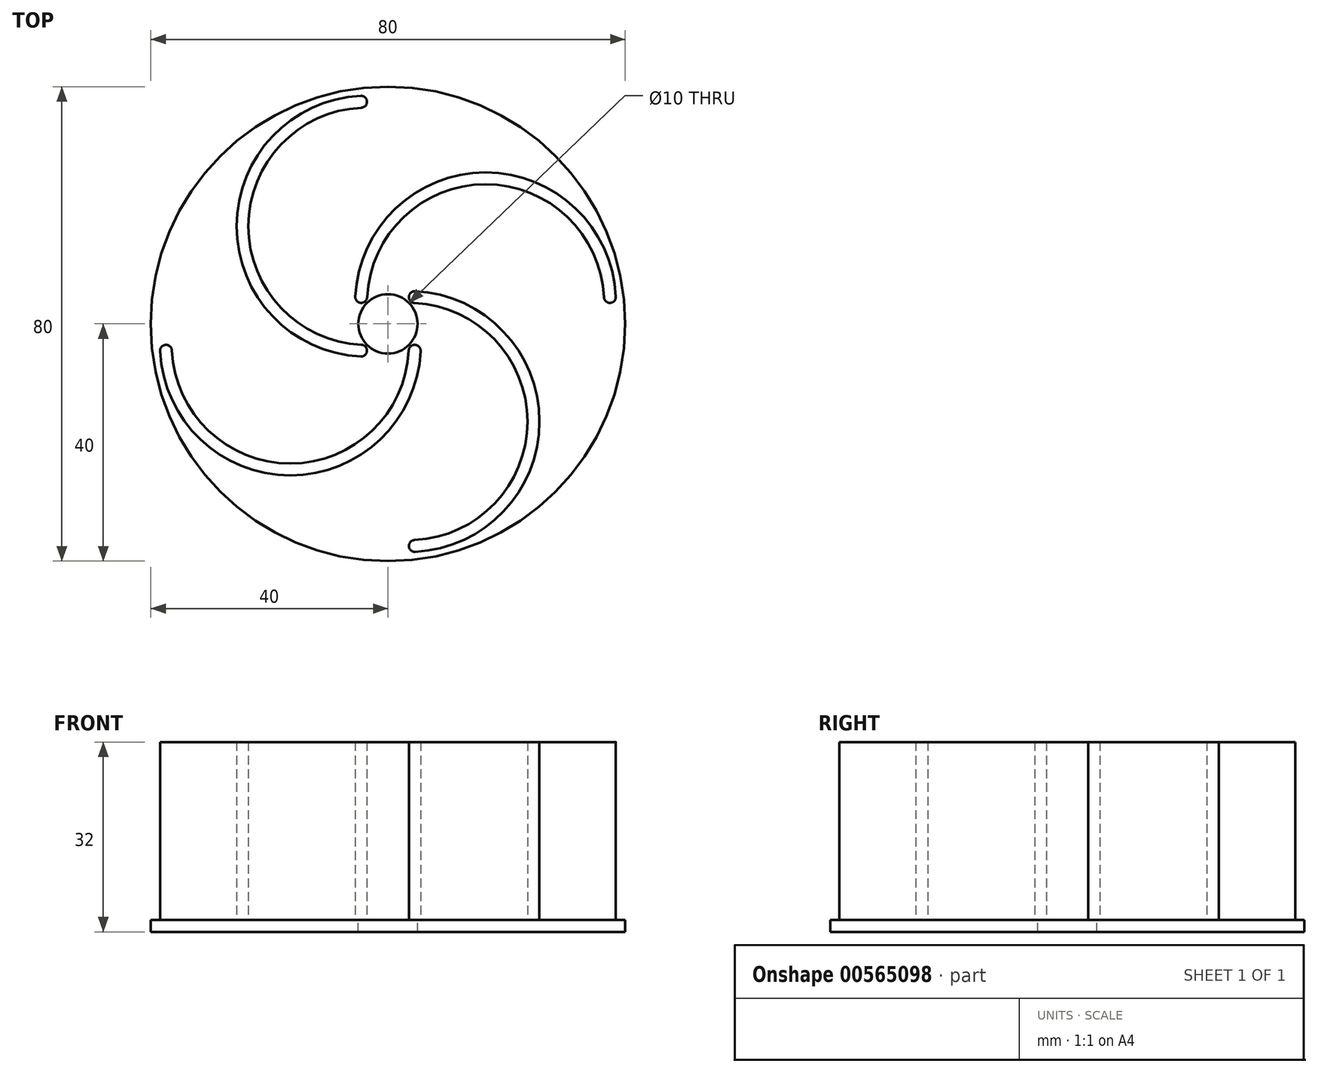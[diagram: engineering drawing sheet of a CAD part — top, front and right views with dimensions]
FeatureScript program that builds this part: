
annotation { "Feature Type Name" : "Feature", "Feature Type Description" : "" }
export const myFeature = defineFeature(function(context is Context, id is Id, definition is map)
    precondition{}
    {
        {
            var Q0;
            Q0=qCreatedBy(makeId("Top.planeOp"),FACE);
            var sketch = newSketch(context, id + "F0", { "sketchPlane" : qUnion([Q0])});
            skCircle(sketch, "E0", {"center": v(0, 0) * mm, "radius": 5 * mm});
            skPoint(sketch, "E1", {"position": v(0, 5) * mm});
            skPoint(sketch, "E2", {"position": v(5, 0) * mm});
            skPoint(sketch, "E3", {"position": v(0, -5) * mm});
            skPoint(sketch, "E4", {"position": v(-5, 0) * mm});
            skLineSegment(sketch, "E5", {"start": v(0, 0) * mm, "end": v(-3.54, -3.54) * mm});
            skLineSegment(sketch, "E6", {"start": v(0, 0) * mm, "end": v(-3.54, 3.54) * mm});
            skLineSegment(sketch, "E7", {"start": v(0, 0) * mm, "end": v(3.54, 3.54) * mm});
            skLineSegment(sketch, "E8", {"start": v(0, 0) * mm, "end": v(3.54, -3.54) * mm});
            skArc(sketch, "E9", {"start": v(3.54, -36.46) * mm, "mid": v(23.54, -16.46) * mm, "end": v(3.54, 3.54) * mm});
            skLineSegment(sketch, "E10", {"start": v(-3.54, -3.54) * mm, "end": v(-3.54, 3.54) * mm});
            skLineSegment(sketch, "E11", {"start": v(3.54, 3.54) * mm, "end": v(3.54, -3.54) * mm});
            skLineSegment(sketch, "E12", {"start": v(3.54, -3.54) * mm, "end": v(-3.54, -3.54) * mm});
            skLineSegment(sketch, "E13", {"start": v(-3.54, 3.54) * mm, "end": v(3.54, 3.54) * mm});
            skArc(sketch, "E14", {"start": v(-3.54, 36.46) * mm, "mid": v(-23.54, 16.46) * mm, "end": v(-3.54, -3.54) * mm});
            skArc(sketch, "E15", {"start": v(36.46, 3.54) * mm, "mid": v(16.46, 23.54) * mm, "end": v(-3.54, 3.54) * mm});
            skArc(sketch, "E16", {"start": v(-36.46, -3.54) * mm, "mid": v(-16.46, -23.54) * mm, "end": v(3.54, -3.54) * mm});
            skArc(sketch, "E17.0", {"start": v(38.46, 3.54) * mm, "mid": v(16.46, 25.54) * mm, "end": v(-5.54, 3.54) * mm});
            skArc(sketch, "E18.0", {"start": v(-3.54, 38.46) * mm, "mid": v(-25.54, 16.46) * mm, "end": v(-3.54, -5.54) * mm});
            skArc(sketch, "E19.0", {"start": v(-38.46, -3.54) * mm, "mid": v(-16.46, -25.54) * mm, "end": v(5.54, -3.54) * mm});
            skArc(sketch, "E20.0", {"start": v(3.54, -38.46) * mm, "mid": v(25.54, -16.46) * mm, "end": v(3.54, 5.54) * mm});
            skLineSegment(sketch, "E21", {"start": v(-3.54, 3.54) * mm, "end": v(-5.54, 3.54) * mm});
            skLineSegment(sketch, "E22", {"start": v(-3.54, -5.54) * mm, "end": v(-3.54, -3.54) * mm});
            skLineSegment(sketch, "E23", {"start": v(5.54, -3.54) * mm, "end": v(3.54, -3.54) * mm});
            skLineSegment(sketch, "E24", {"start": v(3.54, 5.54) * mm, "end": v(3.54, 3.54) * mm});
            skLineSegment(sketch, "E25", {"start": v(38.46, 3.54) * mm, "end": v(36.46, 3.54) * mm});
            skLineSegment(sketch, "E26", {"start": v(-3.54, 38.46) * mm, "end": v(-3.54, 36.46) * mm});
            skLineSegment(sketch, "E27", {"start": v(-38.46, -3.54) * mm, "end": v(-36.46, -3.54) * mm});
            skLineSegment(sketch, "E28", {"start": v(3.54, -36.46) * mm, "end": v(3.54, -38.46) * mm});
            skCircle(sketch, "E29", {"center": v(0, 0) * mm, "radius": 40 * mm});
            skSolve(sketch);
        }
        {
            var Q0;
            Q0=makeQuery(id+"F0.imprint","IMPRINT",FACE,{"disambiguationData":[TD([[makeQuery(id+"F0.imprint","IMPRINT",EDGE,{"derivedFrom":sQuery(id+"F0.wireOp",EDGE,"E15")}),-1.0]])]});
            var Q1;
            Q1=makeQuery(id+"F0.imprint","IMPRINT",FACE,{"disambiguationData":[TD([[makeQuery(id+"F0.imprint","IMPRINT",EDGE,{"derivedFrom":sQuery(id+"F0.wireOp",EDGE,"E9")}),-1.0]])]});
            var Q2;
            Q2=makeQuery(id+"F0.imprint","IMPRINT",FACE,{"disambiguationData":[TD([[makeQuery(id+"F0.imprint","IMPRINT",EDGE,{"derivedFrom":sQuery(id+"F0.wireOp",EDGE,"E14")}),-1.0]])]});
            var Q3;
            Q3=makeQuery(id+"F0.imprint","IMPRINT",FACE,{"disambiguationData":[TD([[makeQuery(id+"F0.imprint","IMPRINT",EDGE,{"derivedFrom":sQuery(id+"F0.wireOp",EDGE,"E16")}),-1.0]])]});
            extrude(context, id + "F1", {"entities" : qUnion([Q0, Q1, Q2, Q3]), "depth" : 30 * mm, "offsetDistance" : 25 * mm});
        }
        {
            var Q0;
            Q0=makeQuery(id+"F1.opExtrude","SWEPT_EDGE",EDGE,{"disambiguationData":[OSD([sQuery(id+"F0.wireOp",EDGE,"E0"),sQuery(id+"F0.wireOp",EDGE,"E6"),sQuery(id+"F0.wireOp",EDGE,"E10"),sQuery(id+"F0.wireOp",EDGE,"E13"),sQuery(id+"F0.wireOp",EDGE,"E15"),sQuery(id+"F0.wireOp",EDGE,"E21")])]});
            var Q1;
            Q1=makeQuery(id+"F1.opExtrude","SWEPT_EDGE",EDGE,{"disambiguationData":[OSD([sQuery(id+"F0.wireOp",EDGE,"E17.0"),sQuery(id+"F0.wireOp",EDGE,"E21")])]});
            var Q2;
            Q2=makeQuery(id+"F1.opExtrude","SWEPT_EDGE",EDGE,{"disambiguationData":[OSD([sQuery(id+"F0.wireOp",EDGE,"E0"),sQuery(id+"F0.wireOp",EDGE,"E7"),sQuery(id+"F0.wireOp",EDGE,"E9"),sQuery(id+"F0.wireOp",EDGE,"E11"),sQuery(id+"F0.wireOp",EDGE,"E13"),sQuery(id+"F0.wireOp",EDGE,"E24")])]});
            var Q3;
            Q3=makeQuery(id+"F1.opExtrude","SWEPT_EDGE",EDGE,{"disambiguationData":[OSD([sQuery(id+"F0.wireOp",EDGE,"E20.0"),sQuery(id+"F0.wireOp",EDGE,"E24")])]});
            var Q4;
            Q4=makeQuery(id+"F1.opExtrude","SWEPT_EDGE",EDGE,{"disambiguationData":[OSD([sQuery(id+"F0.wireOp",EDGE,"E0"),sQuery(id+"F0.wireOp",EDGE,"E8"),sQuery(id+"F0.wireOp",EDGE,"E11"),sQuery(id+"F0.wireOp",EDGE,"E12"),sQuery(id+"F0.wireOp",EDGE,"E16"),sQuery(id+"F0.wireOp",EDGE,"E23")])]});
            var Q5;
            Q5=makeQuery(id+"F1.opExtrude","SWEPT_EDGE",EDGE,{"disambiguationData":[OSD([sQuery(id+"F0.wireOp",EDGE,"E19.0"),sQuery(id+"F0.wireOp",EDGE,"E23")])]});
            var Q6;
            Q6=makeQuery(id+"F1.opExtrude","SWEPT_EDGE",EDGE,{"disambiguationData":[OSD([sQuery(id+"F0.wireOp",EDGE,"E0"),sQuery(id+"F0.wireOp",EDGE,"E5"),sQuery(id+"F0.wireOp",EDGE,"E10"),sQuery(id+"F0.wireOp",EDGE,"E12"),sQuery(id+"F0.wireOp",EDGE,"E14"),sQuery(id+"F0.wireOp",EDGE,"E22")])]});
            var Q7;
            Q7=makeQuery(id+"F1.opExtrude","SWEPT_EDGE",EDGE,{"disambiguationData":[OSD([sQuery(id+"F0.wireOp",EDGE,"E18.0"),sQuery(id+"F0.wireOp",EDGE,"E22")])]});
            var Q8;
            Q8=makeQuery(id+"F1.opExtrude","SWEPT_EDGE",EDGE,{"disambiguationData":[OSD([sQuery(id+"F0.wireOp",EDGE,"E20.0"),sQuery(id+"F0.wireOp",EDGE,"E28")])]});
            var Q9;
            Q9=makeQuery(id+"F1.opExtrude","SWEPT_EDGE",EDGE,{"disambiguationData":[OSD([sQuery(id+"F0.wireOp",EDGE,"E9"),sQuery(id+"F0.wireOp",EDGE,"E28")])]});
            var Q10;
            Q10=makeQuery(id+"F1.opExtrude","SWEPT_EDGE",EDGE,{"disambiguationData":[OSD([sQuery(id+"F0.wireOp",EDGE,"E19.0"),sQuery(id+"F0.wireOp",EDGE,"E27")])]});
            var Q11;
            Q11=makeQuery(id+"F1.opExtrude","SWEPT_EDGE",EDGE,{"disambiguationData":[OSD([sQuery(id+"F0.wireOp",EDGE,"E16"),sQuery(id+"F0.wireOp",EDGE,"E27")])]});
            var Q12;
            Q12=makeQuery(id+"F1.opExtrude","SWEPT_EDGE",EDGE,{"disambiguationData":[OSD([sQuery(id+"F0.wireOp",EDGE,"E18.0"),sQuery(id+"F0.wireOp",EDGE,"E26")])]});
            var Q13;
            Q13=makeQuery(id+"F1.opExtrude","SWEPT_EDGE",EDGE,{"disambiguationData":[OSD([sQuery(id+"F0.wireOp",EDGE,"E14"),sQuery(id+"F0.wireOp",EDGE,"E26")])]});
            var Q14;
            Q14=makeQuery(id+"F1.opExtrude","SWEPT_EDGE",EDGE,{"disambiguationData":[OSD([sQuery(id+"F0.wireOp",EDGE,"E17.0"),sQuery(id+"F0.wireOp",EDGE,"E25")])]});
            var Q15;
            Q15=makeQuery(id+"F1.opExtrude","SWEPT_EDGE",EDGE,{"disambiguationData":[OSD([sQuery(id+"F0.wireOp",EDGE,"E15"),sQuery(id+"F0.wireOp",EDGE,"E25")])]});
            fillet(context, id + "F2", {"entities" : qUnion([Q0, Q1, Q2, Q3, Q4, Q5, Q6, Q7, Q8, Q9, Q10, Q11, Q12, Q13, Q14, Q15]), "radius" : 1 * mm, "tangentPropagation" : true, "allowEdgeOverflow" : false});
        }
        {
            var Q0;
            Q0=qCreatedBy(makeId("Top.planeOp"),FACE);
            var sketch = newSketch(context, id + "F3", { "sketchPlane" : qUnion([Q0])});
            skCircle(sketch, "E30", {"center": v(0, 0) * mm, "radius": 40 * mm});
            skSolve(sketch);
        }
        {
            var Q0;
            Q0=makeQuery(id+"F3.imprint","IMPRINT",FACE,{"disambiguationData":[TD([[makeQuery(id+"F3.imprint","IMPRINT",EDGE,{"derivedFrom":sQuery(id+"F3.wireOp",EDGE,"E30")}),1.0]])]});
            extrude(context, id + "F4", {"entities" : qUnion([Q0]), "oppositeDirection" : true, "depth" : 2 * mm, "offsetDistance" : 25 * mm});
        }
        {
            var Q0;
            Q0=makeQuery(id+"F0.imprint","IMPRINT",FACE,{"disambiguationData":[TD([[makeQuery(id+"F0.imprint","IMPRINT",EDGE,{"derivedFrom":sQuery(id+"F0.wireOp",EDGE,"E5")}),1.0]])]});
            var Q1;
            {var subQ0=sQuery(id+"F0.wireOp",EDGE,"E12");Q1=makeQuery(id+"F0.imprint","IMPRINT",FACE,{"disambiguationData":[TD([[makeQuery(id+"F0.imprint","IMPRINT",EDGE,{"derivedFrom":subQ0}),1.0]])]});}
            var Q2;
            Q2=makeQuery(id+"F0.imprint","IMPRINT",FACE,{"disambiguationData":[TD([[makeQuery(id+"F0.imprint","IMPRINT",EDGE,{"derivedFrom":sQuery(id+"F0.wireOp",EDGE,"E5")}),-1.0]])]});
            var Q3;
            {var subQ0=sQuery(id+"F0.wireOp",EDGE,"E10");Q3=makeQuery(id+"F0.imprint","IMPRINT",FACE,{"disambiguationData":[TD([[makeQuery(id+"F0.imprint","IMPRINT",EDGE,{"derivedFrom":subQ0}),1.0]])]});}
            var Q4;
            Q4=makeQuery(id+"F0.imprint","IMPRINT",FACE,{"disambiguationData":[TD([[makeQuery(id+"F0.imprint","IMPRINT",EDGE,{"derivedFrom":sQuery(id+"F0.wireOp",EDGE,"E6")}),-1.0]])]});
            var Q5;
            {var subQ0=sQuery(id+"F0.wireOp",EDGE,"E13");Q5=makeQuery(id+"F0.imprint","IMPRINT",FACE,{"disambiguationData":[TD([[makeQuery(id+"F0.imprint","IMPRINT",EDGE,{"derivedFrom":subQ0}),1.0]])]});}
            var Q6;
            Q6=makeQuery(id+"F0.imprint","IMPRINT",FACE,{"disambiguationData":[TD([[makeQuery(id+"F0.imprint","IMPRINT",EDGE,{"derivedFrom":sQuery(id+"F0.wireOp",EDGE,"E7")}),-1.0]])]});
            var Q7;
            {var subQ0=sQuery(id+"F0.wireOp",EDGE,"E11");Q7=makeQuery(id+"F0.imprint","IMPRINT",FACE,{"disambiguationData":[TD([[makeQuery(id+"F0.imprint","IMPRINT",EDGE,{"derivedFrom":subQ0}),1.0]])]});}
            extrude(context, id + "F5", {"entities" : qUnion([Q0, Q1, Q2, Q3, Q4, Q5, Q6, Q7]), "operationType" : NewBodyOperationType.REMOVE, "oppositeDirection" : true, "depth" : 25 * mm, "offsetDistance" : 25 * mm});
        }
    });
